# Revit family: QF_ALPENINOX_712666_AJ4R8AAAA
name_source: partatom
category: Specialty Equipment
revit_build: Autodesk Revit 2018 (Build: 20190510_1515(x64)
units: mm (PartAtom-declared; Revit-internal decimal feet)

## family parameters
Always vertical = Yes
Cut with Voids When Loaded = No
Part Type = Normal
Room Calculation Point = No
Round Connector Dimension = Use Diameter
Shared = No
Work Plane-Based = No

## types (1)
- QF_ALPENINOX_712666_AJ4R8AAAA
    Accessory = Yes
    Cold Water Size = 0 mm
    Compressed Air Pressure = 0.0 Pa
    Compressed Air Size = 0 mm
    Compressed Air Volume = 0.0 L/s
    Condensate Return Size = 0 mm
    Cycle = 60 Hz
    Depth = 695 mm  [stored 2.28018 ft]
    Depth Actual = 700 mm  [stored 2.29659 ft]
    Description = 4 DOOR REFRIGERATED TABLE -2C-NO TOP REM
    Gas Input Pressure = 0
    Gas KW = 0
    Gas Size = 0 mm
    HP = 0 HP
    Height = 650 mm  [stored 2.13255 ft]
    Height Actual = 800 mm  [stored 2.62467 ft]
    Hot Water Size = 0 mm
    Item Number = 712666
    Length = 2011 mm  [stored 6.59777 ft]
    Length Actual = 2011 mm  [stored 6.59777 ft]
    Manufacturer = Alpeninox
    Model = AJ4R8AAAA
    Phase = 1
    Refrigerant Compressor Remote = Yes
    Refrigeration Liquid Line Size = 0 mm
    Refrigeration Suction Line Size = 0 mm
    Steam Pounds per Hour = 0
    Steam Supply Maximum Pressure = 0.0 Pa
    Steam Supply Minimum Pressure = 0.0 Pa
    Steam Supply Size = 0 mm
    URL = http://www.alpeninox.com
    URL Manufacturer = http://www.alpeninox.com
    Volts = 220 V
    Watts = 3 W
    Weight = 0.00 kg

note: source unit labels omitted for Gas Input Pressure — the stored unit's dimension contradicts the parameter name (converter mislabeling)

note: [stored X ft] marks values corroborated as IEEE doubles in the binary element streams (Revit-internal decimal feet)

## geometry (parser evidence)
native form markers: Blend x16, Sweep x1
no freeform markers — native parametric forms only
